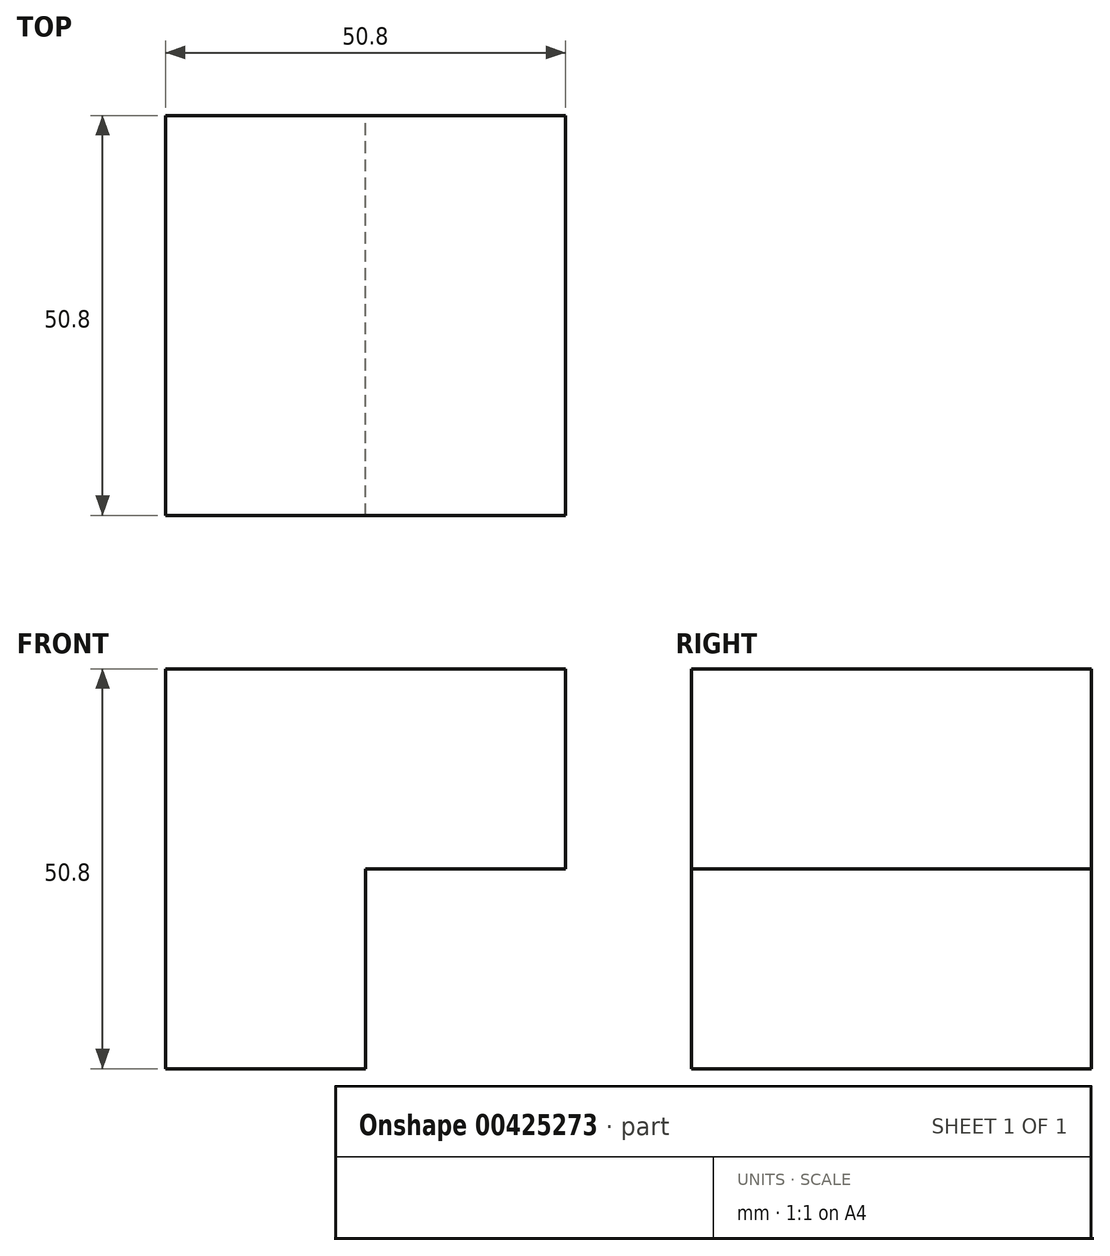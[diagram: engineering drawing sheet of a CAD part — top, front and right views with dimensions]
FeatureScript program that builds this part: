
annotation { "Feature Type Name" : "Feature", "Feature Type Description" : "" }
export const myFeature = defineFeature(function(context is Context, id is Id, definition is map)
    precondition{}
    {
        {
            var Q0;
            Q0=qCreatedBy(makeId("Front.planeOp"),FACE);
            var sketch = newSketch(context, id + "F0", { "sketchPlane" : qUnion([Q0])});
            skLineSegment(sketch, "E0", {"start": v(-25.4, -20.81) * mm, "end": v(-25.4, 29.99) * mm});
            skLineSegment(sketch, "E1", {"start": v(-25.4, 29.99) * mm, "end": v(25.4, 29.99) * mm});
            skLineSegment(sketch, "E2", {"start": v(25.4, 29.99) * mm, "end": v(25.4, 4.59) * mm});
            skLineSegment(sketch, "E3", {"start": v(25.4, 4.59) * mm, "end": v(0, 4.59) * mm});
            skLineSegment(sketch, "E4", {"start": v(0, 4.59) * mm, "end": v(0, -20.81) * mm});
            skLineSegment(sketch, "E5", {"start": v(0, -20.81) * mm, "end": v(-25.4, -20.81) * mm});
            skSolve(sketch);
        }
        {
            var Q0;
            Q0 = qSketchRegion(id + "F0", true);
            extrude(context, id + "F1", {"entities" : qUnion([Q0]), "depth" : 50.8 * mm});
        }
    });
